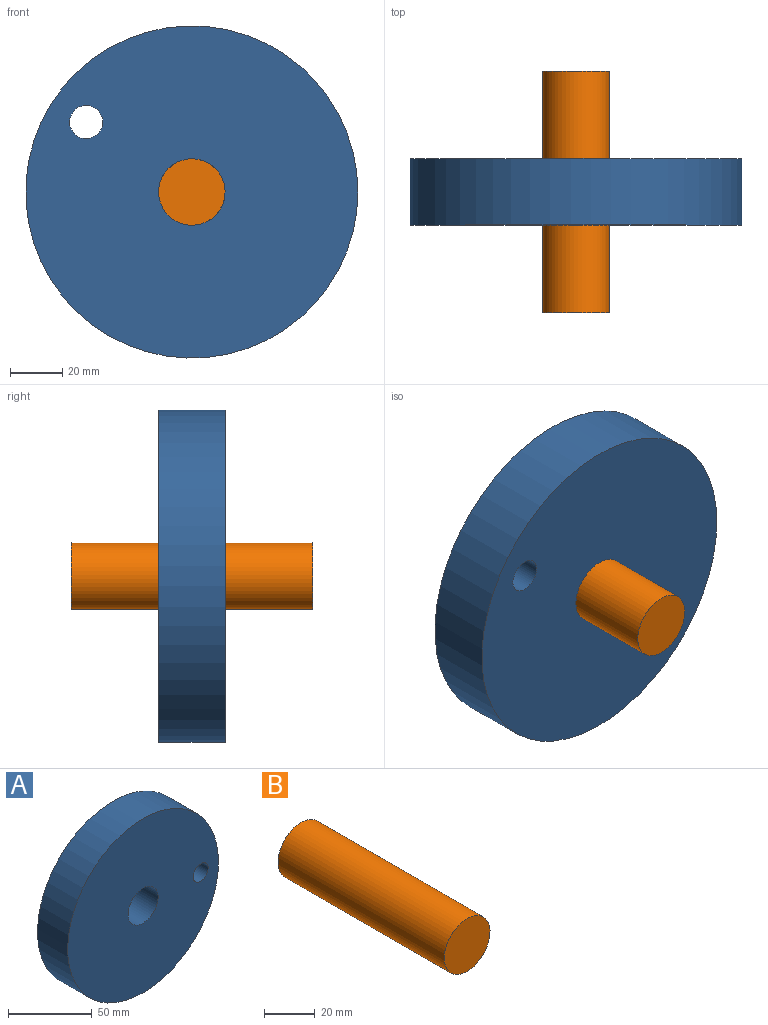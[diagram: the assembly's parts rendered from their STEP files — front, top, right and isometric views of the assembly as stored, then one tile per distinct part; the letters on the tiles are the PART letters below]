
ASSEMBLY  parts=2 mates=1
PART A: 5 faces, bbox 127x25.4x127 mm
  f0: cylinder r=6.35mm len=25.4mm, axis (0,1,0), area 1013.4mm2, adj f3,f4
  f1: cylinder r=12.7mm len=25.4mm, axis (0,1,0), area 2026.8mm2, adj f3,f4
  f2: cylinder r=63.5mm len=127mm, axis (0,1,0), area 10134.1mm2, adj f3,f4
  f3: plane 127x127mm, normal (0,-1,0), area 12034.3mm2, adj f0,f1,f2
  f4: plane 127x127mm, normal (0,1,0), area 12034.3mm2, adj f0,f1,f2
PART B: 3 faces, bbox 25.4x92.3x25.4 mm
  f0: cylinder r=12.7mm len=92.33mm, axis (0,1,0), area 7367.3mm2, adj f1,f2
  f1: plane 25.4x25.4mm, normal (0,-1,0), area 506.7mm2, adj f0
  f2: plane 25.4x25.4mm, normal (0,1,0), area 506.7mm2, adj f0
PLACE A rot(axis=(0,-1,0),146.5deg) t=(-71.18,-27.78,50.42)mm
PLACE B t=(-71.18,5.69,50.42)mm fixed
MATE revolute A.f1 <-> B.f0  axis (0,1,0) through (-71.18,-40.48,50.42)mm
